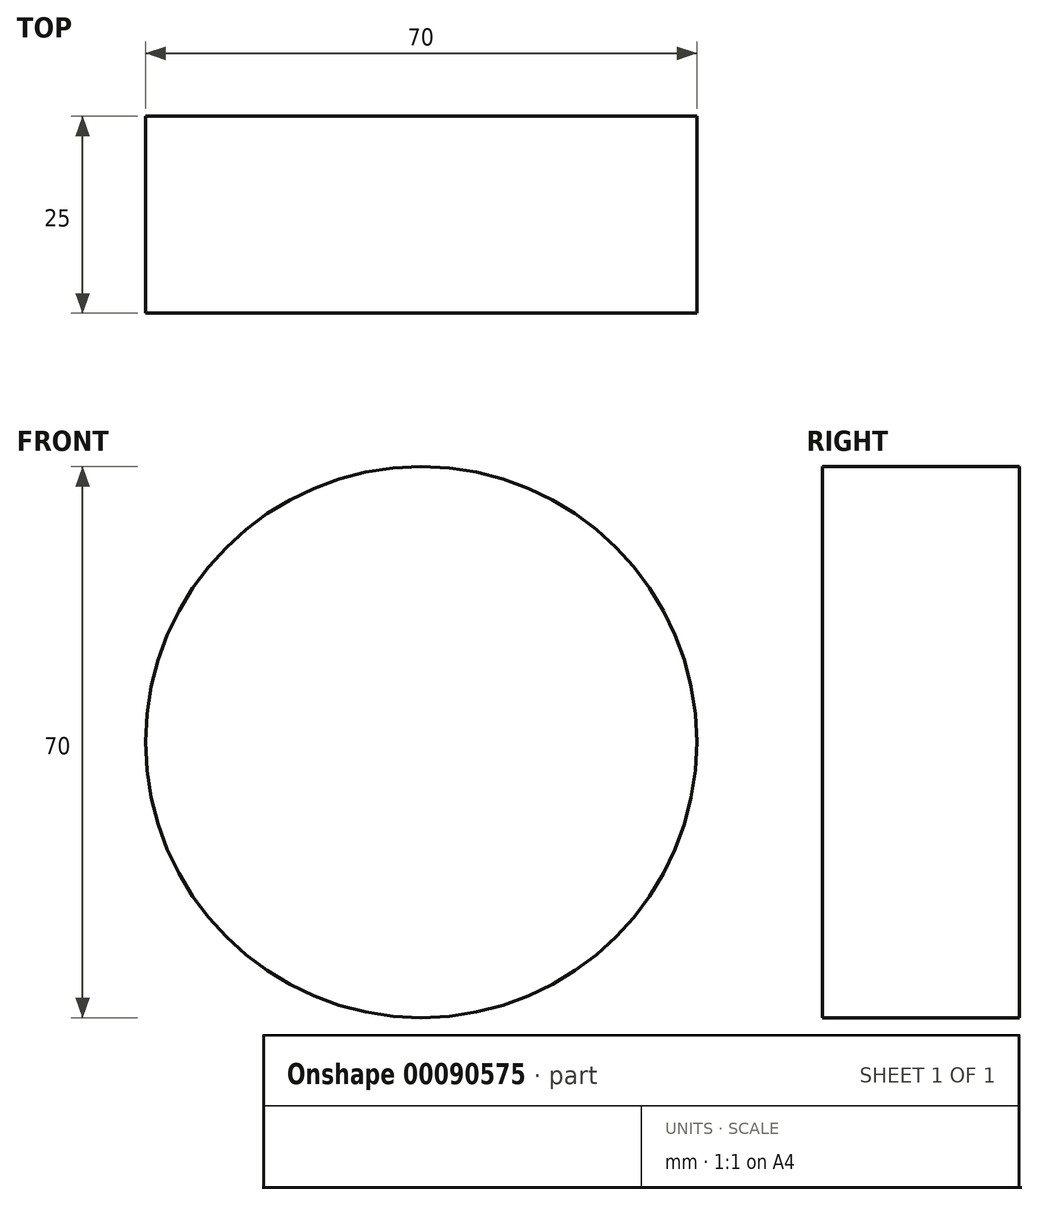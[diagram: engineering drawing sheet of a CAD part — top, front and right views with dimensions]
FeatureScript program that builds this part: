
annotation { "Feature Type Name" : "Feature", "Feature Type Description" : "" }
export const myFeature = defineFeature(function(context is Context, id is Id, definition is map)
    precondition{}
    {
        {
            var Q0;
            Q0=qCreatedBy(makeId("Front.planeOp"),FACE);
            var sketch = newSketch(context, id + "F0", { "sketchPlane" : qUnion([Q0])});
            skCircle(sketch, "E0", {"center": v(0, 0) * mm, "radius": 17 * mm, "construction": true});
            skCircle(sketch, "E1", {"center": v(0, 0) * mm, "radius": 28 * mm, "construction": true});
            skCircle(sketch, "E2", {"center": v(0, 0) * mm, "radius": 14 * mm});
            skCircle(sketch, "E3", {"center": v(0, 0) * mm, "radius": 35 * mm});
            skLineSegment(sketch, "E4", {"start": v(0, 0) * mm, "end": v(12.02, 12.02) * mm, "construction": true});
            skPoint(sketch, "E5", {"position": v(0, 28) * mm});
            skCircle(sketch, "E6", {"center": v(12.02, 12.02) * mm, "radius": 4.12 * mm, "construction": true});
            skCircle(sketch, "E7", {"center": v(0, 28) * mm, "radius": 4.88 * mm, "construction": true});
            skSolve(sketch);
        }
        {
            var Q0;
            Q0=makeQuery(id+"F0.imprint","IMPRINT",FACE,{"disambiguationData":[TD([[makeQuery(id+"F0.imprint","IMPRINT",EDGE,{"derivedFrom":sQuery(id+"F0.wireOp",EDGE,"E2")}),-1.0]])]});
            var Q1;
            Q1=makeQuery(id+"F0.imprint","IMPRINT",FACE,{"disambiguationData":[TD([[makeQuery(id+"F0.imprint","IMPRINT",EDGE,{"derivedFrom":sQuery(id+"F0.wireOp",EDGE,"E2")}),1.0]])]});
            extrude(context, id + "F1", {"entities" : qUnion([Q0, Q1]), "depth" : 25 * mm});
        }
    });
